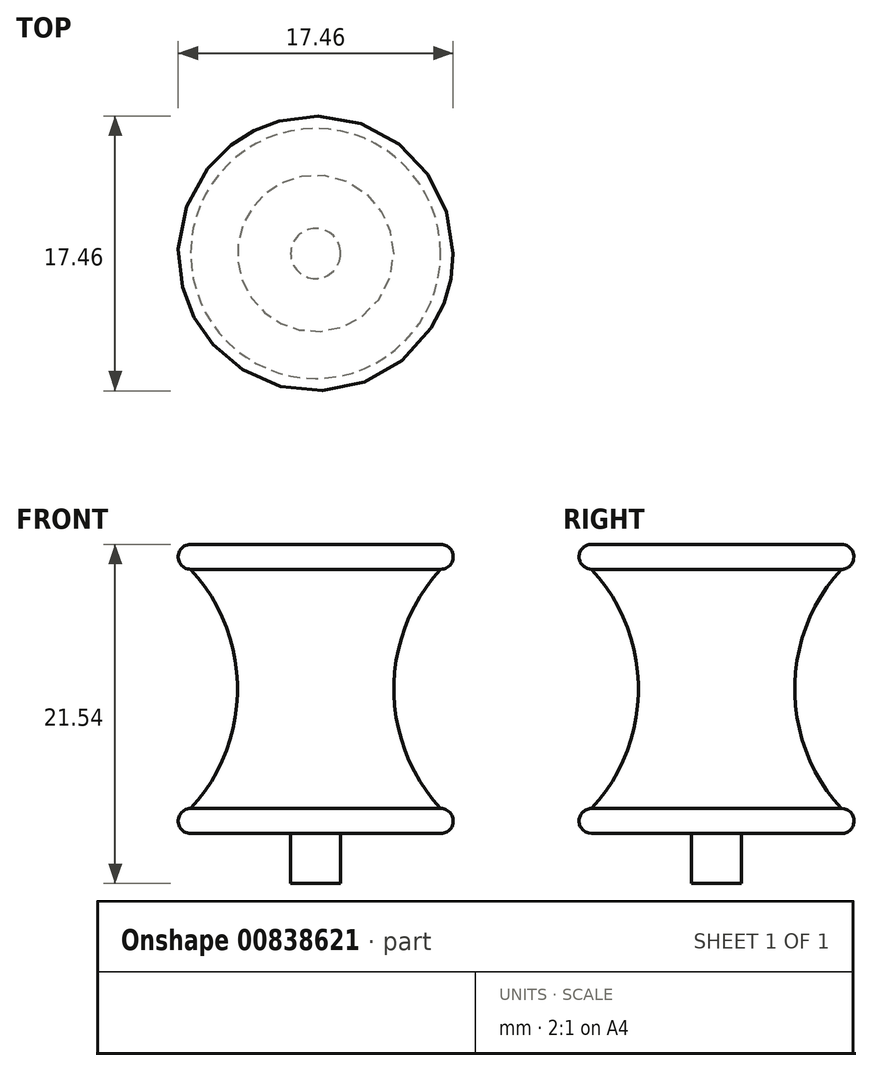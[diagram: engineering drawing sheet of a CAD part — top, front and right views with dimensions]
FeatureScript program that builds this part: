
annotation { "Feature Type Name" : "Feature", "Feature Type Description" : "" }
export const myFeature = defineFeature(function(context is Context, id is Id, definition is map)
    precondition{}
    {
        {
            var Q0;
            Q0=qCreatedBy(makeId("Front.planeOp"),FACE);
            var sketch = newSketch(context, id + "F0", { "sketchPlane" : qUnion([Q0])});
            skLineSegment(sketch, "E0", {"start": v(0, 0) * mm, "end": v(1.59, 0) * mm});
            skLineSegment(sketch, "E1", {"start": v(1.59, 0) * mm, "end": v(1.59, 3.18) * mm});
            skLineSegment(sketch, "E2", {"start": v(0, 21.54) * mm, "end": v(0, 0) * mm});
            skPoint(sketch, "E3.end.orphan", {"position": v(1.59, 10.95) * mm});
            skPoint(sketch, "E4.start.orphan", {"position": v(1.59, 19.96) * mm});
            skLineSegment(sketch, "E5", {"start": v(1.59, 3.18) * mm, "end": v(7.94, 3.18) * mm});
            skLineSegment(sketch, "E6", {"start": v(0, 21.54) * mm, "end": v(7.94, 21.54) * mm});
            skArc(sketch, "E7", {"start": v(7.94, 19.96) * mm, "mid": v(8.73, 20.75) * mm, "end": v(7.94, 21.54) * mm});
            skArc(sketch, "E8", {"start": v(7.94, 3.18) * mm, "mid": v(8.73, 3.97) * mm, "end": v(7.94, 4.76) * mm});
            skArc(sketch, "E9", {"start": v(7.94, 19.96) * mm, "mid": v(4.96, 12.36) * mm, "end": v(7.94, 4.76) * mm});
            skSolve(sketch);
        }
        {
            var Q0;
            Q0=makeQuery(id+"F0.imprint","IMPRINT",FACE,{"disambiguationData":[TD([[makeQuery(id+"F0.imprint","IMPRINT",EDGE,{"derivedFrom":sQuery(id+"F0.wireOp",EDGE,"E0")}),1.0]])]});
            var Q1;
            Q1=sQuery(id+"F0.wireOp",EDGE,"E2");
            revolve(context, id + "F1", {"surfaceOperationType" : NewSurfaceOperationType.NEW, "entities" : qUnion([Q0]), "axis" : qUnion([Q1]), "revolveType" : RevolveType.FULL});
        }
    });
